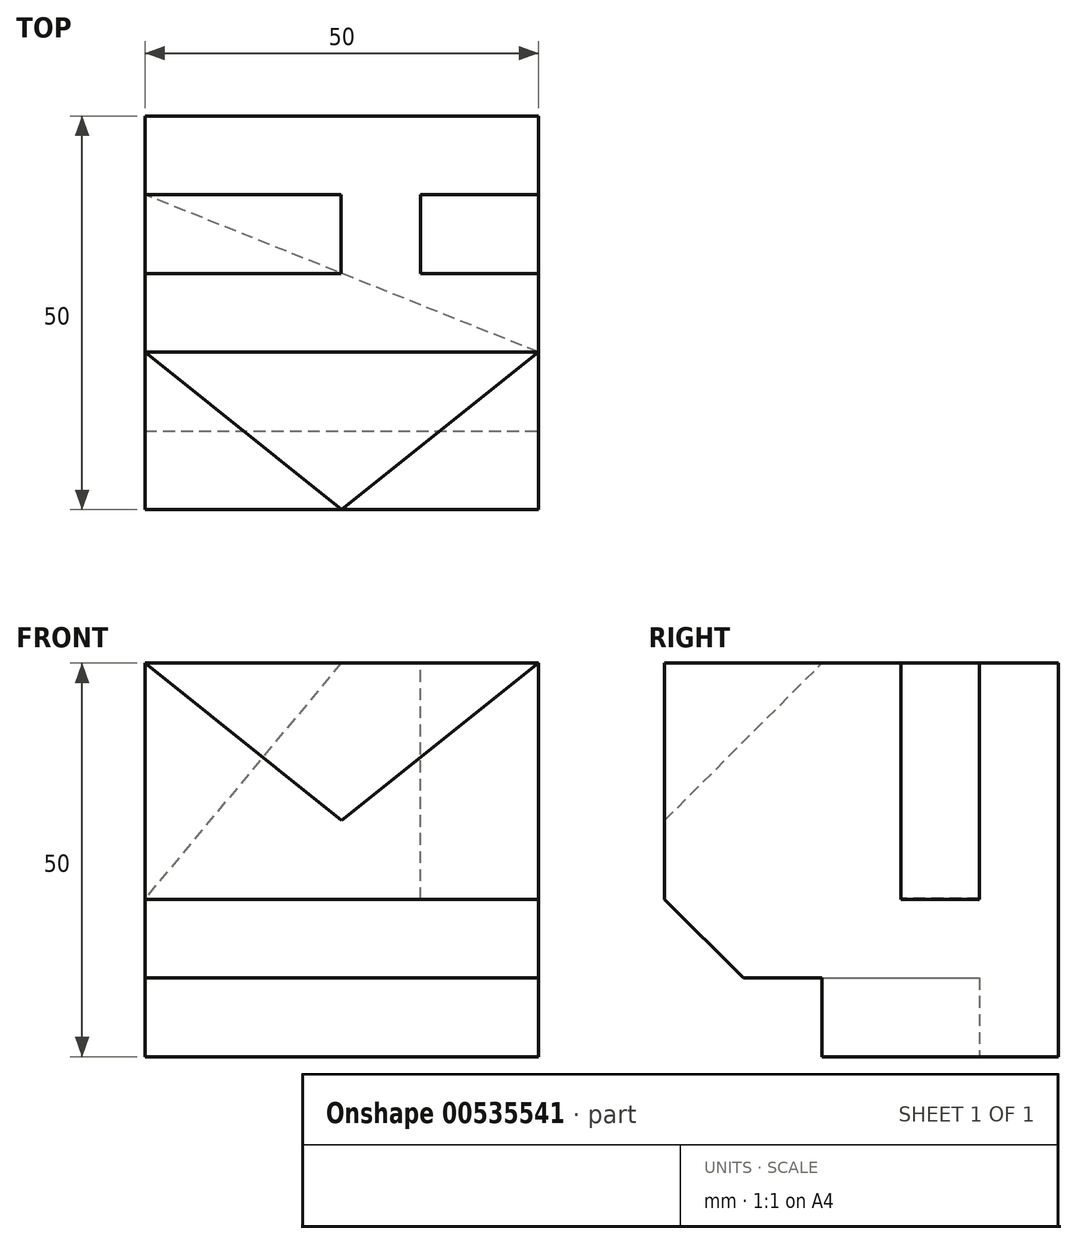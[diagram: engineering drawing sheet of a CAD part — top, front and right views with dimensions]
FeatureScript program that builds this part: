
annotation { "Feature Type Name" : "Feature", "Feature Type Description" : "" }
export const myFeature = defineFeature(function(context is Context, id is Id, definition is map)
    precondition{}
    {
        {
            var Q0;
            Q0=qCreatedBy(makeId("Top.planeOp"),FACE);
            var sketch = newSketch(context, id + "F0", { "sketchPlane" : qUnion([Q0])});
            skLineSegment(sketch, "E0.bottom", {"start": v(0, 0) * mm, "end": v(50, 0) * mm});
            skLineSegment(sketch, "E0.top", {"start": v(0, 50) * mm, "end": v(50, 50) * mm});
            skLineSegment(sketch, "E0.left", {"start": v(0, 0) * mm, "end": v(0, 50) * mm});
            skLineSegment(sketch, "E0.right", {"start": v(50, 0) * mm, "end": v(50, 50) * mm});
            skSolve(sketch);
        }
        {
            var Q0;
            Q0 = qSketchRegion(id + "F0", true);
            extrude(context, id + "F1", {"entities" : qUnion([Q0]), "depth" : 50 * mm, "offsetDistance" : 25 * mm});
        }
        {
            var Q0;
            Q0=makeQuery(id+"F1.opExtrude","CAP_FACE",FACE,{"disambiguationData":[OSD([sQuery(id+"F0.wireOp",EDGE,"E0.bottom"),sQuery(id+"F0.wireOp",EDGE,"E0.top"),sQuery(id+"F0.wireOp",EDGE,"E0.left"),sQuery(id+"F0.wireOp",EDGE,"E0.right")])],"isStart":true});
            var sketch = newSketch(context, id + "F2", { "sketchPlane" : qUnion([Q0])});
            skLineSegment(sketch, "E1.bottom", {"start": v(0, 0) * mm, "end": v(50, 0) * mm});
            skLineSegment(sketch, "E1.top", {"start": v(0, -20) * mm, "end": v(50, -20) * mm});
            skLineSegment(sketch, "E1.left", {"start": v(0, 0) * mm, "end": v(0, -20) * mm});
            skLineSegment(sketch, "E1.right", {"start": v(50, 0) * mm, "end": v(50, -20) * mm});
            skSolve(sketch);
        }
        {
            var Q0;
            Q0 = qSketchRegion(id + "F2", true);
            extrude(context, id + "F3", {"entities" : qUnion([Q0]), "operationType" : NewBodyOperationType.REMOVE, "oppositeDirection" : true, "depth" : 10 * mm, "offsetDistance" : 25 * mm});
        }
        {
            var Q0;
            Q0=makeQuery(id+"F1.opExtrude","CAP_FACE",FACE,{"disambiguationData":[OSD([sQuery(id+"F0.wireOp",EDGE,"E0.bottom"),sQuery(id+"F0.wireOp",EDGE,"E0.top"),sQuery(id+"F0.wireOp",EDGE,"E0.left"),sQuery(id+"F0.wireOp",EDGE,"E0.right")])],"isStart":true});
            var sketch = newSketch(context, id + "F4", { "sketchPlane" : qUnion([Q0])});
            skLineSegment(sketch, "E2", {"start": v(0, -50) * mm, "end": v(0, -40) * mm});
            skLineSegment(sketch, "E3", {"start": v(50, -20) * mm, "end": v(0, -40) * mm});
            skSolve(sketch);
        }
        {
            var Q0;
            Q0 = qSketchRegion(id + "F4", true);
            var Q1;
            {var subQ0=sQuery(id+"F4.wireOp",EDGE,"E3");Q1=makeQuery(id+"F4.imprint","IMPRINT",FACE,{"disambiguationData":[TD([[makeQuery(id+"F4.imprint","IMPRINT",EDGE,{"derivedFrom":subQ0}),-1.0]])]});}
            extrude(context, id + "F5", {"entities" : qUnion([Q0, Q1]), "operationType" : NewBodyOperationType.REMOVE, "oppositeDirection" : true, "depth" : 10 * mm, "offsetDistance" : 25 * mm});
        }
        {
            var Q0;
            Q0=makeQuery(id+"F1.opExtrude","SWEPT_FACE",FACE,{"disambiguationData":[OSD([sQuery(id+"F0.wireOp",EDGE,"E0.right")])]});
            var sketch = newSketch(context, id + "F6", { "sketchPlane" : qUnion([Q0])});
            skLineSegment(sketch, "E4", {"start": v(0, 10) * mm, "end": v(10, 10) * mm});
            skLineSegment(sketch, "E5", {"start": v(0, 10) * mm, "end": v(0, 20) * mm});
            skLineSegment(sketch, "E6", {"start": v(0, 20) * mm, "end": v(10, 10) * mm});
            skSolve(sketch);
        }
        {
            var Q0;
            Q0 = qSketchRegion(id + "F6", true);
            extrude(context, id + "F7", {"entities" : qUnion([Q0]), "operationType" : NewBodyOperationType.REMOVE, "endBound" : BoundingType.UP_TO_NEXT, "oppositeDirection" : true, "depth" : 25 * mm, "offsetDistance" : 25 * mm});
        }
        {
            var Q0;
            Q0=qCreatedBy(makeId("Front.planeOp"),FACE);
            cPlane(context, id + "F8", {"entities" : qUnion([Q0]), "cplaneType" : CPlaneType.OFFSET, "offset" : 30 * mm, "oppositeDirection" : true, "width" : 150 * mm, "height" : 150 * mm});
        }
        {
            var Q0;
            Q0=qCreatedBy(id+"F8.planeOp",FACE);
            var sketch = newSketch(context, id + "F9", { "sketchPlane" : qUnion([Q0])});
            skLineSegment(sketch, "E7", {"start": v(0, 50.09) * mm, "end": v(0, 20.09) * mm});
            skLineSegment(sketch, "E8", {"start": v(0, 50.09) * mm, "end": v(25, 50.09) * mm});
            skLineSegment(sketch, "E9", {"start": v(25, 50.09) * mm, "end": v(0, 20.09) * mm});
            skSolve(sketch);
        }
        {
            var Q0;
            Q0 = qSketchRegion(id + "F9", true);
            extrude(context, id + "F10", {"entities" : qUnion([Q0]), "operationType" : NewBodyOperationType.REMOVE, "oppositeDirection" : true, "depth" : 10 * mm, "offsetDistance" : 25 * mm});
        }
        {
            var Q0;
            Q0=makeQuery(id+"F1.opExtrude","CAP_FACE",FACE,{"disambiguationData":[OSD([sQuery(id+"F0.wireOp",EDGE,"E0.bottom"),sQuery(id+"F0.wireOp",EDGE,"E0.top"),sQuery(id+"F0.wireOp",EDGE,"E0.left"),sQuery(id+"F0.wireOp",EDGE,"E0.right")])],"isStart":false});
            var sketch = newSketch(context, id + "F11", { "sketchPlane" : qUnion([Q0])});
            skLineSegment(sketch, "E10", {"start": v(50, 50) * mm, "end": v(50, 40) * mm});
            skLineSegment(sketch, "E11", {"start": v(50, 40) * mm, "end": v(50, 30) * mm});
            skLineSegment(sketch, "E12", {"start": v(50, 30) * mm, "end": v(50, 35) * mm});
            skLineSegment(sketch, "E13", {"start": v(50, 40) * mm, "end": v(35, 40) * mm});
            skLineSegment(sketch, "E14", {"start": v(35, 40) * mm, "end": v(35, 30) * mm});
            skLineSegment(sketch, "E15", {"start": v(35, 30) * mm, "end": v(50, 30) * mm});
            skSolve(sketch);
        }
        {
            var Q0;
            Q0 = qSketchRegion(id + "F11", true);
            extrude(context, id + "F12", {"entities" : qUnion([Q0]), "operationType" : NewBodyOperationType.REMOVE, "oppositeDirection" : true, "depth" : 30 * mm, "offsetDistance" : 25 * mm});
        }
        {
            var Q0;
            Q0=makeQuery(id+"F1.opExtrude","SWEPT_FACE",FACE,{"disambiguationData":[OSD([sQuery(id+"F0.wireOp",EDGE,"E0.bottom")])]});
            var sketch = newSketch(context, id + "F13", { "sketchPlane" : qUnion([Q0])});
            skLineSegment(sketch, "E16", {"start": v(0, 50) * mm, "end": v(0, 30) * mm});
            skLineSegment(sketch, "E17", {"start": v(0, 30) * mm, "end": v(25, 30) * mm});
            skLineSegment(sketch, "E18", {"start": v(0, 50) * mm, "end": v(25, 30) * mm});
            skLineSegment(sketch, "E19", {"start": v(50, 50) * mm, "end": v(25, 30) * mm});
            skLineSegment(sketch, "E20", {"start": v(50, 50) * mm, "end": v(0, 50) * mm});
            skSolve(sketch);
        }
        {
            var Q0;
            Q0=makeQuery(id+"F1.opExtrude","CAP_FACE",FACE,{"disambiguationData":[OSD([sQuery(id+"F0.wireOp",EDGE,"E0.bottom"),sQuery(id+"F0.wireOp",EDGE,"E0.top"),sQuery(id+"F0.wireOp",EDGE,"E0.left"),sQuery(id+"F0.wireOp",EDGE,"E0.right")])],"isStart":false});
            var sketch = newSketch(context, id + "F14", { "sketchPlane" : qUnion([Q0])});
            skLineSegment(sketch, "E21", {"start": v(0, 0) * mm, "end": v(0, 20) * mm});
            skLineSegment(sketch, "E22", {"start": v(50, 0) * mm, "end": v(50, 20) * mm});
            skSolve(sketch);
        }
        {
            var Q0;
            Q0=sQuery(id+"F14.wireOp",VERTEX,"E21.end");
            var Q1;
            Q1=sQuery(id+"F14.wireOp",VERTEX,"E22.end");
            var Q2;
            Q2=sQuery(id+"F13.wireOp",VERTEX,"E16.end");
            cPlane(context, id + "F15", {"entities" : qUnion([Q0, Q1, Q2]), "cplaneType" : CPlaneType.THREE_POINT, "offset" : 25 * mm, "width" : 150 * mm, "height" : 150 * mm});
        }
        {
            var Q0;
            Q0=makeQuery(id+"F13.imprint","IMPRINT",FACE,{"disambiguationData":[TD([[makeQuery(id+"F13.imprint","IMPRINT",EDGE,{"derivedFrom":sQuery(id+"F13.wireOp",EDGE,"E18")}),1.0]])]});
            var Q1;
            Q1=qCreatedBy(id+"F15.planeOp",FACE);
            extrude(context, id + "F16", {"entities" : qUnion([Q0]), "operationType" : NewBodyOperationType.REMOVE, "endBound" : BoundingType.UP_TO_SURFACE, "oppositeDirection" : true, "depth" : 25 * mm, "endBoundEntityFace" : qUnion([Q1]), "offsetDistance" : 25 * mm});
        }
    });
